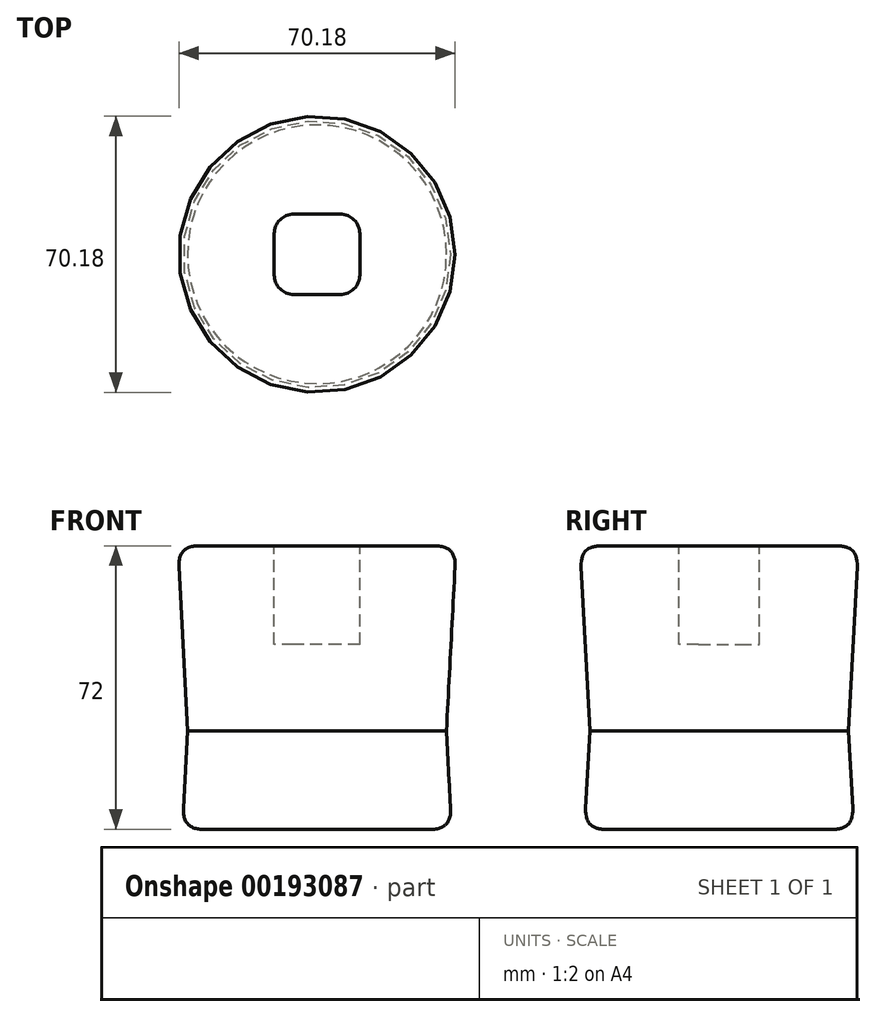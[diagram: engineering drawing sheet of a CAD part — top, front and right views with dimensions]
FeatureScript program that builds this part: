
annotation { "Feature Type Name" : "Feature", "Feature Type Description" : "" }
export const myFeature = defineFeature(function(context is Context, id is Id, definition is map)
    precondition{}
    {
        {
            var Q0;
            Q0=qCreatedBy(makeId("Top.planeOp"),FACE);
            var sketch = newSketch(context, id + "F0", { "sketchPlane" : qUnion([Q0])});
            skCircle(sketch, "E0", {"center": v(0, 0) * mm, "radius": 32.89 * mm});
            skSolve(sketch);
        }
        {
            var Q0;
            Q0 = qSketchRegion(id + "F0", true);
            extrude(context, id + "F1", {"entities" : qUnion([Q0]), "depth" : 47 * mm, "hasDraft" : true, "draftAngle" : 3 * degree, "hasSecondDirection" : true, "secondDirectionOppositeDirection" : true, "secondDirectionDepth" : 25 * mm, "hasSecondDirectionDraft" : true, "secondDirectionDraftAngle" : 3 * degree});
        }
        {
            var Q0;
            Q0=makeQuery(id+"F1.opExtrude","CAP_EDGE",EDGE,{"disambiguationData":[OSD([sQuery(id+"F0.wireOp",EDGE,"E0")])],"isStart":false});
            var Q1;
            Q1=makeQuery(id+"F1.opExtrude","CAP_EDGE",EDGE,{"disambiguationData":[OSD([sQuery(id+"F0.wireOp",EDGE,"E0")])],"isStart":true});
            fillet(context, id + "F2", {"entities" : qUnion([Q0, Q1]), "radius" : 5 * mm, "tangentPropagation" : true, "rho" : 0.5, "crossSection" : FilletCrossSection.CONIC, "allowEdgeOverflow" : false});
        }
        {
            var Q0;
            Q0=makeQuery(id+"F1.opExtrude","CAP_FACE",FACE,{"disambiguationData":[OSD([sQuery(id+"F0.wireOp",EDGE,"E0")])],"isStart":false});
            var sketch = newSketch(context, id + "F3", { "sketchPlane" : qUnion([Q0])});
            skLineSegment(sketch, "E1.bottom", {"start": v(5.87, -10.21) * mm, "end": v(-5.87, -10.21) * mm});
            skLineSegment(sketch, "E1.top", {"start": v(5.87, 10.21) * mm, "end": v(-5.87, 10.21) * mm});
            skLineSegment(sketch, "E1.left", {"start": v(10.87, -5.21) * mm, "end": v(10.87, 5.21) * mm});
            skLineSegment(sketch, "E1.right", {"start": v(-10.87, -5.21) * mm, "end": v(-10.87, 5.21) * mm});
            skPoint(sketch, "E1.middle", {"position": v(0, 0) * mm});
            skPoint(sketch, "E2.visualSharp", {"position": v(-10.87, 10.21) * mm});
            skArc(sketch, "E2.filletArc", {"start": v(-5.87, 10.21) * mm, "mid": v(-9.4, 8.75) * mm, "end": v(-10.87, 5.21) * mm});
            skPoint(sketch, "E3.visualSharp", {"position": v(10.87, 10.21) * mm});
            skArc(sketch, "E3.filletArc", {"start": v(10.87, 5.21) * mm, "mid": v(9.4, 8.75) * mm, "end": v(5.87, 10.21) * mm});
            skPoint(sketch, "E4.visualSharp", {"position": v(10.87, -10.21) * mm});
            skArc(sketch, "E4.filletArc", {"start": v(5.87, -10.21) * mm, "mid": v(9.4, -8.75) * mm, "end": v(10.87, -5.21) * mm});
            skPoint(sketch, "E5.visualSharp", {"position": v(-10.87, -10.21) * mm});
            skArc(sketch, "E5.filletArc", {"start": v(-10.87, -5.21) * mm, "mid": v(-9.4, -8.75) * mm, "end": v(-5.87, -10.21) * mm});
            skSolve(sketch);
        }
        {
            var Q0;
            Q0=makeQuery(id+"F3.imprint","IMPRINT",FACE,{"disambiguationData":[TD([[makeQuery(id+"F3.imprint","IMPRINT",EDGE,{"derivedFrom":sQuery(id+"F3.wireOp",EDGE,"E1.bottom")}),-1.0]])]});
            extrude(context, id + "F4", {"entities" : qUnion([Q0]), "operationType" : NewBodyOperationType.REMOVE, "oppositeDirection" : true, "depth" : 25 * mm});
        }
    });
